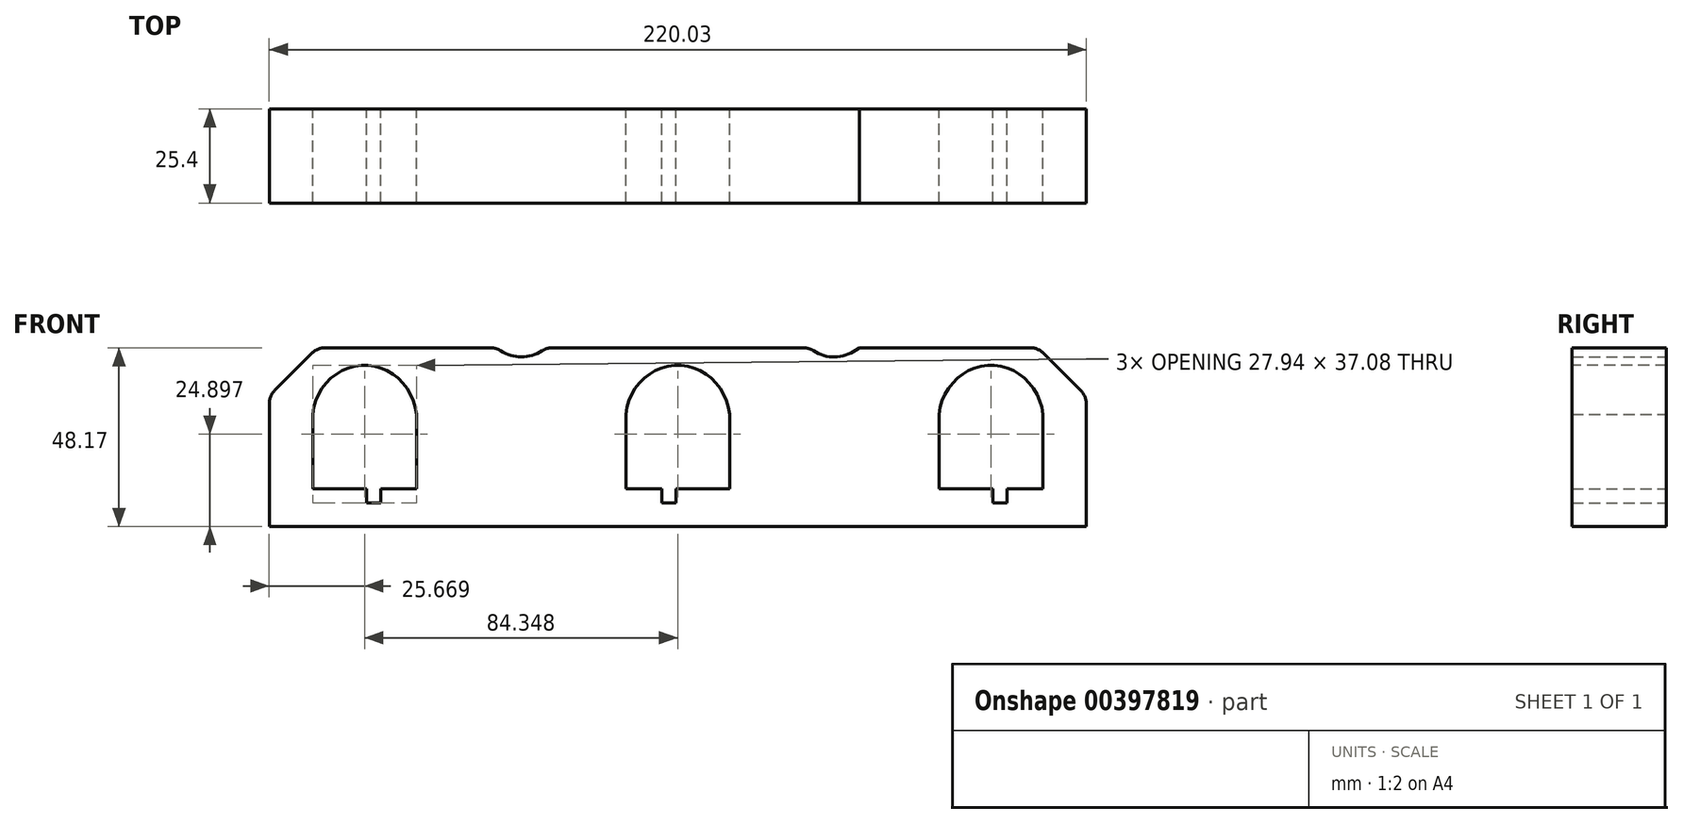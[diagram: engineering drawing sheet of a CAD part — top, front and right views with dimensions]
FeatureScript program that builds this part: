
annotation { "Feature Type Name" : "Feature", "Feature Type Description" : "" }
export const myFeature = defineFeature(function(context is Context, id is Id, definition is map)
    precondition{}
    {
        {
            var Q0;
            Q0=qCreatedBy(makeId("Front.planeOp"),FACE);
            var sketch = newSketch(context, id + "F0", { "sketchPlane" : qUnion([Q0])});
            skLineSegment(sketch, "E0.0", {"start": v(-52.02, 5) * mm, "end": v(-52.02, 25.07) * mm});
            skLineSegment(sketch, "E0.1", {"start": v(-52.02, 5) * mm, "end": v(-66.5, 5) * mm});
            skLineSegment(sketch, "E0.2", {"start": v(-70.31, 5) * mm, "end": v(-79.96, 5) * mm});
            skLineSegment(sketch, "E0.3", {"start": v(-79.96, 25.07) * mm, "end": v(-79.96, 5) * mm});
            skLineSegment(sketch, "E0.4", {"start": v(-70.31, 5) * mm, "end": v(-70.31, 1.2) * mm});
            skLineSegment(sketch, "E0.5", {"start": v(-66.5, 5) * mm, "end": v(-66.5, 1.2) * mm});
            skLineSegment(sketch, "E0.6", {"start": v(-70.31, 1.2) * mm, "end": v(-66.5, 1.2) * mm});
            skEllipticalArc(sketch, "E0.7", {});
            skEllipticalArc(sketch, "E0.8", {});
            skEllipticalArc(sketch, "E0.9", {});
            skEllipticalArc(sketch, "E0.10", {});
            skLineSegment(sketch, "E1.bottom", {"start": v(-26.37, -5.16) * mm, "end": v(-105.62, -5.16) * mm});
            skLineSegment(sketch, "E1.top", {"start": v(-26.37, 51.61) * mm, "end": v(-105.62, 51.61) * mm});
            skLineSegment(sketch, "E1.left", {"start": v(-26.37, -5.16) * mm, "end": v(-26.37, 51.61) * mm});
            skLineSegment(sketch, "E1.right", {"start": v(-105.62, -5.16) * mm, "end": v(-105.62, 51.61) * mm});
            skLineSegment(sketch, "E2", {"start": v(-59.64, 36.68) * mm, "end": v(-72.34, 36.68) * mm, "construction": true});
            const initialGuessF0  = {"E0.7": [-0.06599263550790663, 0.023481545698889272, 0, 1, 0.01479728219747515, 0.014051279666989923, 4.820000208360302, 5.814273145917696], "E0.8": [-0.06599263550790663, 0.023481545698889272, 0, 1, 0.01479728219747515, 0.014051279666989923, 5.814273145917696, 0], "E0.9": [-0.06599263550790663, 0.023481545698889272, 0, 1, 0.01479728219747515, 0.014051279666989923, 0, 0.4689121612618875], "E0.10": [-0.06599263550790663, 0.023481545698889272, 0, 1, 0.01479728219747515, 0.014051279666989923, 0.4689121612618875, 1.4631850988192838]};
            skSetInitialGuess(sketch, initialGuessF0);
            skSolve(sketch);
        }
        {
            var Q0;
            Q0=makeQuery(id+"F0.imprint","IMPRINT",FACE,{"disambiguationData":[TD([[makeQuery(id+"F0.imprint","IMPRINT",EDGE,{"derivedFrom":sQuery(id+"F0.wireOp",EDGE,"E0.0")}),-1.0]])]});
            extrude(context, id + "F1", {"entities" : qUnion([Q0]), "depth" : 25.4 * mm});
        }
        {
            var Q0;
            Q0=makeQuery(id+"F1.opExtrude","CAP_FACE",FACE,{"disambiguationData":[OSD([sQuery(id+"F0.wireOp",EDGE,"E0.0"),sQuery(id+"F0.wireOp",EDGE,"E0.1"),sQuery(id+"F0.wireOp",EDGE,"E0.2"),sQuery(id+"F0.wireOp",EDGE,"E0.3"),sQuery(id+"F0.wireOp",EDGE,"E0.4"),sQuery(id+"F0.wireOp",EDGE,"E0.5"),sQuery(id+"F0.wireOp",EDGE,"E0.6"),sQuery(id+"F0.wireOp",EDGE,"E0.7"),sQuery(id+"F0.wireOp",EDGE,"E0.8"),sQuery(id+"F0.wireOp",EDGE,"E0.9"),sQuery(id+"F0.wireOp",EDGE,"E0.10"),sQuery(id+"F0.wireOp",EDGE,"E1.bottom"),sQuery(id+"F0.wireOp",EDGE,"E1.top"),sQuery(id+"F0.wireOp",EDGE,"E1.left"),sQuery(id+"F0.wireOp",EDGE,"E1.right")])],"isStart":false});
            var sketch = newSketch(context, id + "F2", { "sketchPlane" : qUnion([Q0])});
            skLineSegment(sketch, "E3.bottom", {"start": v(-105.62, 51.61) * mm, "end": v(-108.17, 51.61) * mm});
            skLineSegment(sketch, "E3.top", {"start": v(-105.62, -5.16) * mm, "end": v(-108.17, -5.16) * mm});
            skLineSegment(sketch, "E3.left", {"start": v(-105.62, 51.61) * mm, "end": v(-105.62, -5.16) * mm});
            skLineSegment(sketch, "E3.right", {"start": v(-108.17, 51.61) * mm, "end": v(-108.17, -5.16) * mm});
            skLineSegment(sketch, "E4.bottom", {"start": v(-26.37, 51.61) * mm, "end": v(-23.82, 51.61) * mm});
            skLineSegment(sketch, "E4.top", {"start": v(-26.37, -5.16) * mm, "end": v(-23.82, -5.16) * mm});
            skLineSegment(sketch, "E4.left", {"start": v(-26.37, 51.61) * mm, "end": v(-26.37, -5.16) * mm});
            skLineSegment(sketch, "E4.right", {"start": v(-23.82, 51.61) * mm, "end": v(-23.82, -5.16) * mm});
            skSolve(sketch);
        }
        {
            var Q0;
            Q0 = qSketchRegion(id + "F2", true);
            var Q1;
            Q1=makeQuery(id+"F1.opExtrude","CAP_FACE",FACE,{"disambiguationData":[OSD([sQuery(id+"F0.wireOp",EDGE,"E0.0"),sQuery(id+"F0.wireOp",EDGE,"E0.1"),sQuery(id+"F0.wireOp",EDGE,"E0.2"),sQuery(id+"F0.wireOp",EDGE,"E0.3"),sQuery(id+"F0.wireOp",EDGE,"E0.4"),sQuery(id+"F0.wireOp",EDGE,"E0.5"),sQuery(id+"F0.wireOp",EDGE,"E0.6"),sQuery(id+"F0.wireOp",EDGE,"E0.7"),sQuery(id+"F0.wireOp",EDGE,"E0.8"),sQuery(id+"F0.wireOp",EDGE,"E0.9"),sQuery(id+"F0.wireOp",EDGE,"E0.10"),sQuery(id+"F0.wireOp",EDGE,"E1.bottom"),sQuery(id+"F0.wireOp",EDGE,"E1.top"),sQuery(id+"F0.wireOp",EDGE,"E1.left"),sQuery(id+"F0.wireOp",EDGE,"E1.right")])],"isStart":true});
            extrude(context, id + "F3", {"entities" : qUnion([Q0]), "operationType" : NewBodyOperationType.ADD, "endBound" : BoundingType.UP_TO_SURFACE, "oppositeDirection" : true, "endBoundEntityFace" : qUnion([Q1]), "depth" : 25.4 * mm});
        }
        {
            var Q0;
            Q0=makeQuery(id+"F1.opExtrude","SWEPT_BODY",BODY,{"disambiguationData":[OSD([sQuery(id+"F0.wireOp",EDGE,"E0.0"),sQuery(id+"F0.wireOp",EDGE,"E0.1"),sQuery(id+"F0.wireOp",EDGE,"E0.2"),sQuery(id+"F0.wireOp",EDGE,"E0.3"),sQuery(id+"F0.wireOp",EDGE,"E0.4"),sQuery(id+"F0.wireOp",EDGE,"E0.5"),sQuery(id+"F0.wireOp",EDGE,"E0.6"),sQuery(id+"F0.wireOp",EDGE,"E0.7"),sQuery(id+"F0.wireOp",EDGE,"E0.8"),sQuery(id+"F0.wireOp",EDGE,"E0.9"),sQuery(id+"F0.wireOp",EDGE,"E0.10"),sQuery(id+"F0.wireOp",EDGE,"E1.bottom"),sQuery(id+"F0.wireOp",EDGE,"E1.top"),sQuery(id+"F0.wireOp",EDGE,"E1.left"),sQuery(id+"F0.wireOp",EDGE,"E1.right")])]});
            var Q1;
            Q1=makeQuery(id+"F3.opExtrude","SWEPT_FACE",FACE,{"disambiguationData":[OSD([sQuery(id+"F2.wireOp",EDGE,"E3.right")])]});
            mirror(context, id + "F4", {"operationType" : NewBodyOperationType.ADD, "entities" : qUnion([Q0]), "mirrorPlane" : qUnion([Q1])});
        }
        {
            var Q0;
            Q0=makeQuery(id+"F1.opExtrude","SWEPT_BODY",BODY,{"disambiguationData":[OSD([sQuery(id+"F0.wireOp",EDGE,"E0.0"),sQuery(id+"F0.wireOp",EDGE,"E0.1"),sQuery(id+"F0.wireOp",EDGE,"E0.2"),sQuery(id+"F0.wireOp",EDGE,"E0.3"),sQuery(id+"F0.wireOp",EDGE,"E0.4"),sQuery(id+"F0.wireOp",EDGE,"E0.5"),sQuery(id+"F0.wireOp",EDGE,"E0.6"),sQuery(id+"F0.wireOp",EDGE,"E0.7"),sQuery(id+"F0.wireOp",EDGE,"E0.8"),sQuery(id+"F0.wireOp",EDGE,"E0.9"),sQuery(id+"F0.wireOp",EDGE,"E0.10"),sQuery(id+"F0.wireOp",EDGE,"E1.bottom"),sQuery(id+"F0.wireOp",EDGE,"E1.top"),sQuery(id+"F0.wireOp",EDGE,"E1.left"),sQuery(id+"F0.wireOp",EDGE,"E1.right")])]});
            var Q1;
            Q1=makeQuery(id+"F3.opExtrude","SWEPT_FACE",FACE,{"disambiguationData":[OSD([sQuery(id+"F2.wireOp",EDGE,"E4.right")])]});
            mirror(context, id + "F5", {"operationType" : NewBodyOperationType.ADD, "entities" : qUnion([Q0]), "mirrorPlane" : qUnion([Q1])});
        }
        {
            var Q0;
            {var subQ0=makeQuery(id+"F3.boolean.opBoolean","MERGE",FACE,{"derivedFrom":[makeQuery(id+"F1.opExtrude","CAP_FACE",FACE,{"disambiguationData":[OSD([sQuery(id+"F0.wireOp",EDGE,"E0.0"),sQuery(id+"F0.wireOp",EDGE,"E0.1"),sQuery(id+"F0.wireOp",EDGE,"E0.2"),sQuery(id+"F0.wireOp",EDGE,"E0.3"),sQuery(id+"F0.wireOp",EDGE,"E0.4"),sQuery(id+"F0.wireOp",EDGE,"E0.5"),sQuery(id+"F0.wireOp",EDGE,"E0.6"),sQuery(id+"F0.wireOp",EDGE,"E0.7"),sQuery(id+"F0.wireOp",EDGE,"E0.8"),sQuery(id+"F0.wireOp",EDGE,"E0.9"),sQuery(id+"F0.wireOp",EDGE,"E0.10"),sQuery(id+"F0.wireOp",EDGE,"E1.bottom"),sQuery(id+"F0.wireOp",EDGE,"E1.top"),sQuery(id+"F0.wireOp",EDGE,"E1.left"),sQuery(id+"F0.wireOp",EDGE,"E1.right")])],"isStart":false}),makeQuery(id+"F3.opExtrude","CAP_FACE",FACE,{"disambiguationData":[OSD([sQuery(id+"F2.wireOp",EDGE,"E3.bottom"),sQuery(id+"F2.wireOp",EDGE,"E3.top"),sQuery(id+"F2.wireOp",EDGE,"E3.left"),sQuery(id+"F2.wireOp",EDGE,"E3.right")])],"isStart":true}),makeQuery(id+"F3.opExtrude","CAP_FACE",FACE,{"disambiguationData":[OSD([sQuery(id+"F2.wireOp",EDGE,"E4.bottom"),sQuery(id+"F2.wireOp",EDGE,"E4.top"),sQuery(id+"F2.wireOp",EDGE,"E4.left"),sQuery(id+"F2.wireOp",EDGE,"E4.right")])],"isStart":true})]});var subQ1=makeQuery(id+"F4.boolean.opBoolean","MERGE",FACE,{"derivedFrom":[subQ0,makeQuery(id+"F4.opPattern","COPY",FACE,{"derivedFrom":subQ0,"instanceName":"1"})]});Q0=makeQuery(id+"F5.boolean.opBoolean","MERGE",FACE,{"derivedFrom":[subQ1,makeQuery(id+"F5.opPattern","COPY",FACE,{"derivedFrom":subQ1,"instanceName":"1"})]});}
            var sketch = newSketch(context, id + "F6", { "sketchPlane" : qUnion([Q0])});
            skLineSegment(sketch, "E5", {"start": v(-23.82, 51.61) * mm, "end": v(-23.82, -5.16) * mm, "construction": true});
            skSolve(sketch);
        }
        {
            var Q0;
            {var subQ4=makeQuery(id+"F1.opExtrude","CAP_EDGE",EDGE,{"disambiguationData":[OSD([sQuery(id+"F0.wireOp",EDGE,"E0.0")])],"isStart":false});Q0=makeQuery(id+"F6.imprint","IMPRINT",FACE,{"disambiguationData":[TD([[makeQuery(id+"F6.imprint","IMPRINT",EDGE,{"derivedFrom":subQ4}),-1.0]])]});}
            var sketch = newSketch(context, id + "F7", { "sketchPlane" : qUnion([Q0])});
            skLineSegment(sketch, "E6", {"start": v(60.53, 51.61) * mm, "end": v(60.53, -5.16) * mm});
            skLineSegment(sketch, "E7", {"start": v(60.53, 51.61) * mm, "end": v(144.88, 51.61) * mm});
            skLineSegment(sketch, "E8", {"start": v(144.88, 51.61) * mm, "end": v(144.88, -5.16) * mm});
            skLineSegment(sketch, "E9", {"start": v(144.88, -5.16) * mm, "end": v(60.53, -5.16) * mm});
            skSolve(sketch);
        }
        {
            var Q0;
            Q0 = qSketchRegion(id + "F7", true);
            extrude(context, id + "F8", {"entities" : qUnion([Q0]), "operationType" : NewBodyOperationType.REMOVE, "endBound" : BoundingType.THROUGH_ALL, "oppositeDirection" : true, "depth" : 25.4 * mm});
        }
        {
            var Q0;
            {var subQ4=makeQuery(id+"F1.opExtrude","CAP_EDGE",EDGE,{"disambiguationData":[OSD([sQuery(id+"F0.wireOp",EDGE,"E0.0")])],"isStart":false});Q0=makeQuery(id+"F6.imprint","IMPRINT",FACE,{"disambiguationData":[TD([[makeQuery(id+"F6.imprint","IMPRINT",EDGE,{"derivedFrom":subQ4}),-1.0]])]});}
            var sketch = newSketch(context, id + "F9", { "sketchPlane" : qUnion([Q0])});
            skLineSegment(sketch, "E10.bottom", {"start": v(60.53, 51.61) * mm, "end": v(44.02, 51.61) * mm});
            skLineSegment(sketch, "E10.top", {"start": v(60.53, -5.16) * mm, "end": v(44.02, -5.16) * mm});
            skLineSegment(sketch, "E10.left", {"start": v(60.53, 51.61) * mm, "end": v(60.53, -5.16) * mm});
            skLineSegment(sketch, "E10.right", {"start": v(44.02, 30.02) * mm, "end": v(44.02, -5.16) * mm});
            skLineSegment(sketch, "E11.bottom", {"start": v(-192.52, 51.61) * mm, "end": v(-176, 51.61) * mm});
            skLineSegment(sketch, "E11.top", {"start": v(-192.52, -5.16) * mm, "end": v(-176, -5.16) * mm});
            skLineSegment(sketch, "E11.left", {"start": v(-192.52, 51.61) * mm, "end": v(-192.52, -5.16) * mm});
            skLineSegment(sketch, "E11.right", {"start": v(-176, 30.02) * mm, "end": v(-176, -5.16) * mm});
            skLineSegment(sketch, "E12.bottom", {"start": v(-176, 51.61) * mm, "end": v(44.02, 51.61) * mm});
            skLineSegment(sketch, "E12.top", {"start": v(-163.02, 43) * mm, "end": v(31.04, 43) * mm});
            skLineSegment(sketch, "E13", {"start": v(-176, 30.02) * mm, "end": v(-163.02, 43) * mm});
            skLineSegment(sketch, "E14", {"start": v(-163.02, 43) * mm, "end": v(-133.58, 43) * mm});
            skLineSegment(sketch, "E15", {"start": v(31.04, 43) * mm, "end": v(44.02, 30.02) * mm});
            skSolve(sketch);
        }
        {
            var Q0;
            Q0 = qSketchRegion(id + "F9", true);
            extrude(context, id + "F10", {"entities" : qUnion([Q0]), "operationType" : NewBodyOperationType.REMOVE, "endBound" : BoundingType.THROUGH_ALL, "oppositeDirection" : true, "depth" : 25.4 * mm});
        }
        {
            var Q0;
            {var subQ4=makeQuery(id+"F1.opExtrude","CAP_EDGE",EDGE,{"disambiguationData":[OSD([sQuery(id+"F0.wireOp",EDGE,"E0.0")])],"isStart":false});Q0=makeQuery(id+"F6.imprint","IMPRINT",FACE,{"disambiguationData":[TD([[makeQuery(id+"F6.imprint","IMPRINT",EDGE,{"derivedFrom":subQ4}),-1.0]])]});}
            var sketch = newSketch(context, id + "F11", { "sketchPlane" : qUnion([Q0])});
            skLineSegment(sketch, "E16", {"start": v(-108.1, 43) * mm, "end": v(-108.1, -5.16) * mm, "construction": true});
            skLineSegment(sketch, "E17", {"start": v(-23.88, 43) * mm, "end": v(-23.88, -5.16) * mm, "construction": true});
            skLineSegment(sketch, "E18", {"start": v(-105.61, 43) * mm, "end": v(-108.1, 40.52) * mm, "construction": true});
            skLineSegment(sketch, "E19", {"start": v(-108.1, 40.52) * mm, "end": v(-110.59, 43) * mm, "construction": true});
            skLineSegment(sketch, "E20", {"start": v(-23.88, 40.52) * mm, "end": v(-26.37, 43) * mm, "construction": true});
            skLineSegment(sketch, "E21", {"start": v(-23.88, 40.52) * mm, "end": v(-21.4, 43) * mm, "construction": true});
            skLineSegment(sketch, "E22", {"start": v(-110.59, 43) * mm, "end": v(-105.61, 43) * mm, "construction": true});
            skLineSegment(sketch, "E23", {"start": v(-26.37, 43) * mm, "end": v(-21.4, 43) * mm, "construction": true});
            skLineSegment(sketch, "E24", {"start": v(-23.88, 38.28) * mm, "end": v(-30.64, 43) * mm});
            skLineSegment(sketch, "E25.MirrorCS", {"start": v(-23.88, 38.28) * mm, "end": v(-17.13, 43) * mm});
            skLineSegment(sketch, "E26", {"start": v(-30.64, 43) * mm, "end": v(-17.13, 43) * mm});
            skLineSegment(sketch, "E27", {"start": v(-108.1, 38.28) * mm, "end": v(-101.34, 43) * mm});
            skLineSegment(sketch, "E28", {"start": v(-101.34, 43) * mm, "end": v(-114.86, 43) * mm});
            skLineSegment(sketch, "E29", {"start": v(-114.86, 43) * mm, "end": v(-108.1, 38.28) * mm});
            skSolve(sketch);
        }
        {
            var Q0;
            Q0 = qSketchRegion(id + "F11", true);
            extrude(context, id + "F12", {"entities" : qUnion([Q0]), "operationType" : NewBodyOperationType.REMOVE, "endBound" : BoundingType.THROUGH_ALL, "oppositeDirection" : true, "depth" : 25.4 * mm});
        }
        {
            var Q0;
            Q0=makeQuery(id+"F12.boolean.opBoolean","COPY",EDGE,{"derivedFrom":makeQuery(id+"F12.opExtrude","SWEPT_EDGE",EDGE,{"disambiguationData":[OSD([sQuery(id+"F11.wireOp",EDGE,"E24"),sQuery(id+"F11.wireOp",EDGE,"E25.MirrorCS")])]})});
            var Q1;
            Q1=makeQuery(id+"F12.boolean.opBoolean","COPY",EDGE,{"derivedFrom":makeQuery(id+"F12.opExtrude","SWEPT_EDGE",EDGE,{"disambiguationData":[OSD([sQuery(id+"F11.wireOp",EDGE,"E27"),sQuery(id+"F11.wireOp",EDGE,"E29")])]})});
            fillet(context, id + "F13", {"entities" : qUnion([Q0, Q1]), "radius" : 10.16 * mm, "tangentPropagation" : true, "allowEdgeOverflow" : false});
        }
        {
            var Q0;
            Q0=makeQuery(id+"F12.boolean.opBoolean","COPY",EDGE,{"derivedFrom":makeQuery(id+"F12.opExtrude","SWEPT_EDGE",EDGE,{"disambiguationData":[OSD([sQuery(id+"F11.wireOp",EDGE,"E25.MirrorCS"),sQuery(id+"F11.wireOp",EDGE,"E26")])]})});
            var Q1;
            Q1=makeQuery(id+"F12.boolean.opBoolean","COPY",EDGE,{"derivedFrom":makeQuery(id+"F12.opExtrude","SWEPT_EDGE",EDGE,{"disambiguationData":[OSD([sQuery(id+"F11.wireOp",EDGE,"E24"),sQuery(id+"F11.wireOp",EDGE,"E26")])]})});
            var Q2;
            Q2=makeQuery(id+"F12.boolean.opBoolean","COPY",EDGE,{"derivedFrom":makeQuery(id+"F12.opExtrude","SWEPT_EDGE",EDGE,{"disambiguationData":[OSD([sQuery(id+"F11.wireOp",EDGE,"E27"),sQuery(id+"F11.wireOp",EDGE,"E28")])]})});
            var Q3;
            Q3=makeQuery(id+"F12.boolean.opBoolean","COPY",EDGE,{"derivedFrom":makeQuery(id+"F12.opExtrude","SWEPT_EDGE",EDGE,{"disambiguationData":[OSD([sQuery(id+"F11.wireOp",EDGE,"E28"),sQuery(id+"F11.wireOp",EDGE,"E29")])]})});
            var Q4;
            Q4=makeQuery(id+"F10.boolean.opBoolean","COPY",EDGE,{"derivedFrom":makeQuery(id+"F10.opExtrude","SWEPT_EDGE",EDGE,{"disambiguationData":[OSD([sQuery(id+"F9.wireOp",EDGE,"E13"),sQuery(id+"F9.wireOp",EDGE,"E14")])]})});
            var Q5;
            Q5=makeQuery(id+"F10.boolean.opBoolean","COPY",EDGE,{"derivedFrom":makeQuery(id+"F10.opExtrude","SWEPT_EDGE",EDGE,{"disambiguationData":[OSD([sQuery(id+"F9.wireOp",EDGE,"E11.right"),sQuery(id+"F9.wireOp",EDGE,"E13")])]})});
            var Q6;
            Q6=makeQuery(id+"F10.boolean.opBoolean","COPY",EDGE,{"derivedFrom":makeQuery(id+"F10.opExtrude","SWEPT_EDGE",EDGE,{"disambiguationData":[OSD([sQuery(id+"F9.wireOp",EDGE,"E12.top"),sQuery(id+"F9.wireOp",EDGE,"E15")])]})});
            var Q7;
            Q7=makeQuery(id+"F10.boolean.opBoolean","COPY",EDGE,{"derivedFrom":makeQuery(id+"F10.opExtrude","SWEPT_EDGE",EDGE,{"disambiguationData":[OSD([sQuery(id+"F9.wireOp",EDGE,"E10.right"),sQuery(id+"F9.wireOp",EDGE,"E15")])]})});
            var Q8;
            Q8=makeQuery(id+"F10.boolean.opBoolean","COPY",EDGE,{"derivedFrom":makeQuery(id+"F10.opExtrude","SWEPT_EDGE",EDGE,{"disambiguationData":[OSD([sQuery(id+"F0.wireOp",EDGE,"E1.bottom"),sQuery(id+"F2.wireOp",EDGE,"E3.top"),sQuery(id+"F2.wireOp",EDGE,"E4.top"),sQuery(id+"F9.wireOp",EDGE,"E10.top"),sQuery(id+"F9.wireOp",EDGE,"E10.right")])]})});
            var Q9;
            Q9=makeQuery(id+"F10.boolean.opBoolean","COPY",EDGE,{"derivedFrom":makeQuery(id+"F10.opExtrude","SWEPT_EDGE",EDGE,{"disambiguationData":[OSD([sQuery(id+"F0.wireOp",EDGE,"E1.bottom"),sQuery(id+"F2.wireOp",EDGE,"E3.top"),sQuery(id+"F2.wireOp",EDGE,"E4.top"),sQuery(id+"F9.wireOp",EDGE,"E11.top"),sQuery(id+"F9.wireOp",EDGE,"E11.right")])]})});
            fillet(context, id + "F14", {"entities" : qUnion([Q0, Q1, Q2, Q3, Q4, Q5, Q6, Q7, Q8, Q9]), "radius" : 5.08 * mm, "tangentPropagation" : true, "allowEdgeOverflow" : false});
        }
    });
